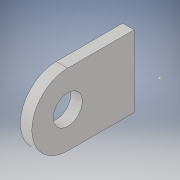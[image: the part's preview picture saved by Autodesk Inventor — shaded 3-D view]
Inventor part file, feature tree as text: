
AUTODESK INVENTOR PART (.ipt)
format: ipt  version: 2019 (Build 230136000, 136)  size: 115,712 bytes
history: native  units: mm
features: sketch x3, other x1, extrude x1, hole x1
ambient origin geometry x8: Origin, YZ Plane, XZ Plane, XY Plane, X Axis, Y Axis, Z Axis, Center Point
bodies: Body1 (feature_tree)
feature tree (6):
  other  "ソリッド1"
  extrude  "押し出し1"  Depth=8.1mm
  sketch  "スケッチ2"
  hole  "穴1"  [1 undecoded]
  sketch  "スケッチ1"
  sketch  "スケッチ3"
note: 1 required parameter value undecoded (feature->parameter linkage not recoverable at this tier; creation-order binding heuristic only, values carry confidence <= 0.55)
